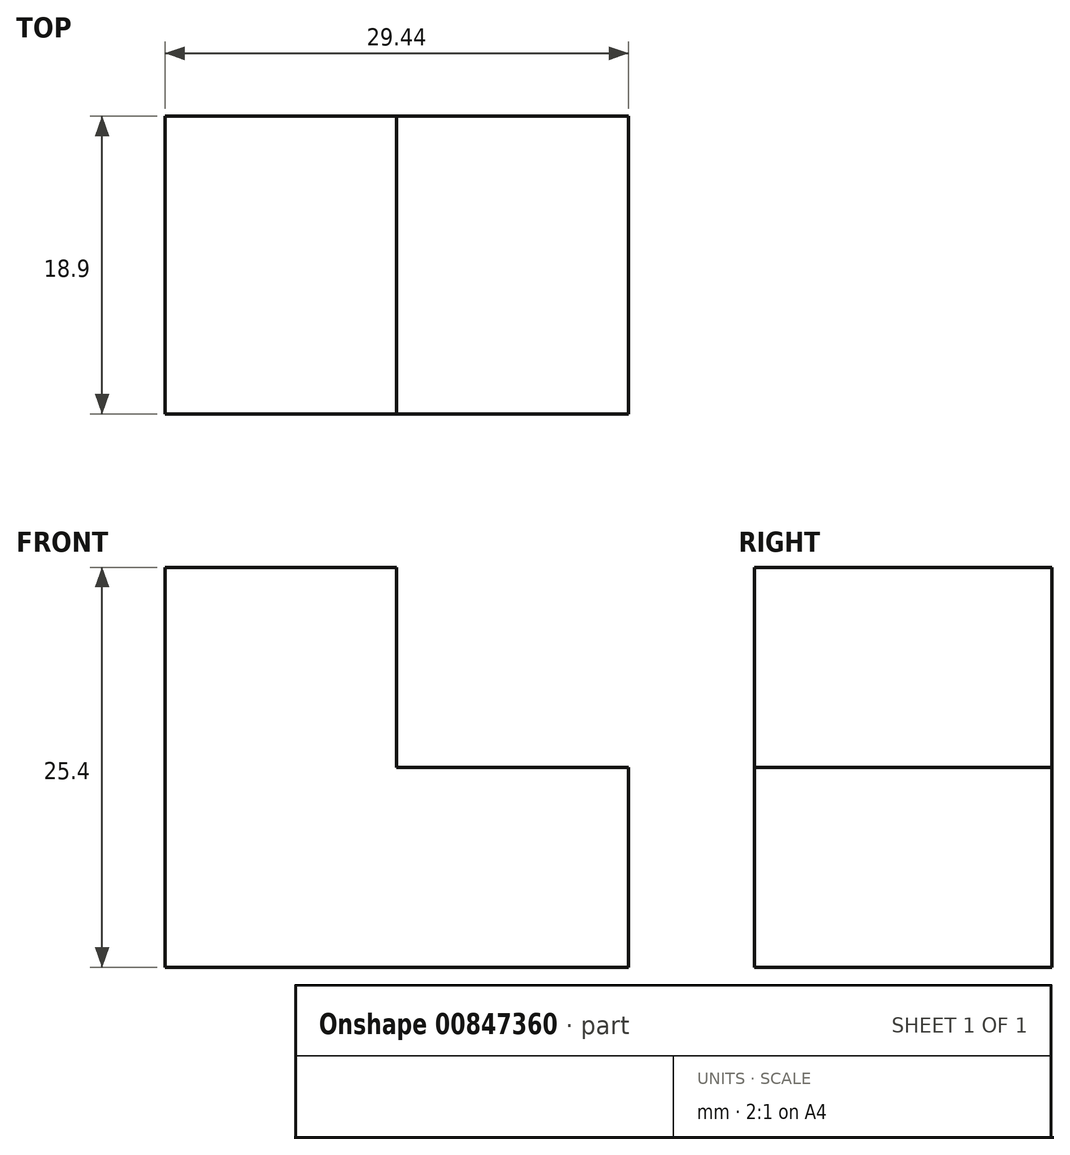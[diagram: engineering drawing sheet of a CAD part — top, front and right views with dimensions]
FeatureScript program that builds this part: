
annotation { "Feature Type Name" : "Feature", "Feature Type Description" : "" }
export const myFeature = defineFeature(function(context is Context, id is Id, definition is map)
    precondition{}
    {
        {
            var Q0;
            Q0=qCreatedBy(makeId("Top.planeOp"),FACE);
            var sketch = newSketch(context, id + "F0", { "sketchPlane" : qUnion([Q0])});
            skLineSegment(sketch, "E0.bottom", {"start": v(14.72, -9.45) * mm, "end": v(-14.72, -9.45) * mm});
            skLineSegment(sketch, "E0.top", {"start": v(14.72, 9.45) * mm, "end": v(-14.72, 9.45) * mm});
            skLineSegment(sketch, "E0.left", {"start": v(14.72, -9.45) * mm, "end": v(14.72, 9.45) * mm});
            skLineSegment(sketch, "E0.right", {"start": v(-14.72, -9.45) * mm, "end": v(-14.72, 9.45) * mm});
            skPoint(sketch, "E0.middle", {"position": v(0, 0) * mm});
            skLineSegment(sketch, "E1", {"start": v(0, 0) * mm, "end": v(-14.72, 0) * mm});
            skSolve(sketch);
        }
        {
            var Q0;
            Q0 = qSketchRegion(id + "F0", true);
            extrude(context, id + "F1", {"entities" : qUnion([Q0]), "depth" : 12.7 * mm, "offsetDistance" : 25.4 * mm});
        }
        {
            var Q0;
            Q0=makeQuery(id+"F1.opExtrude","CAP_FACE",FACE,{"disambiguationData":[OSD([sQuery(id+"F0.wireOp",EDGE,"E0.bottom"),sQuery(id+"F0.wireOp",EDGE,"E0.top"),sQuery(id+"F0.wireOp",EDGE,"E0.left"),sQuery(id+"F0.wireOp",EDGE,"E0.right")])],"isStart":false});
            var sketch = newSketch(context, id + "F2", { "sketchPlane" : qUnion([Q0])});
            skLineSegment(sketch, "E2", {"start": v(0, 0) * mm, "end": v(-14.72, 0) * mm});
            skLineSegment(sketch, "E3.bottom", {"start": v(0, -9.45) * mm, "end": v(-14.72, -9.45) * mm});
            skLineSegment(sketch, "E3.top", {"start": v(0, 9.45) * mm, "end": v(-14.72, 9.45) * mm});
            skLineSegment(sketch, "E3.left", {"start": v(0, -9.45) * mm, "end": v(0, 9.45) * mm});
            skLineSegment(sketch, "E3.right", {"start": v(-14.72, -9.45) * mm, "end": v(-14.72, 9.45) * mm});
            skPoint(sketch, "E3.middle", {"position": v(-7.36, 0) * mm});
            skSolve(sketch);
        }
        {
            var Q0;
            Q0 = qSketchRegion(id + "F2", true);
            extrude(context, id + "F3", {"entities" : qUnion([Q0]), "operationType" : NewBodyOperationType.ADD, "depth" : 12.7 * mm, "offsetDistance" : 25.4 * mm});
        }
    });
